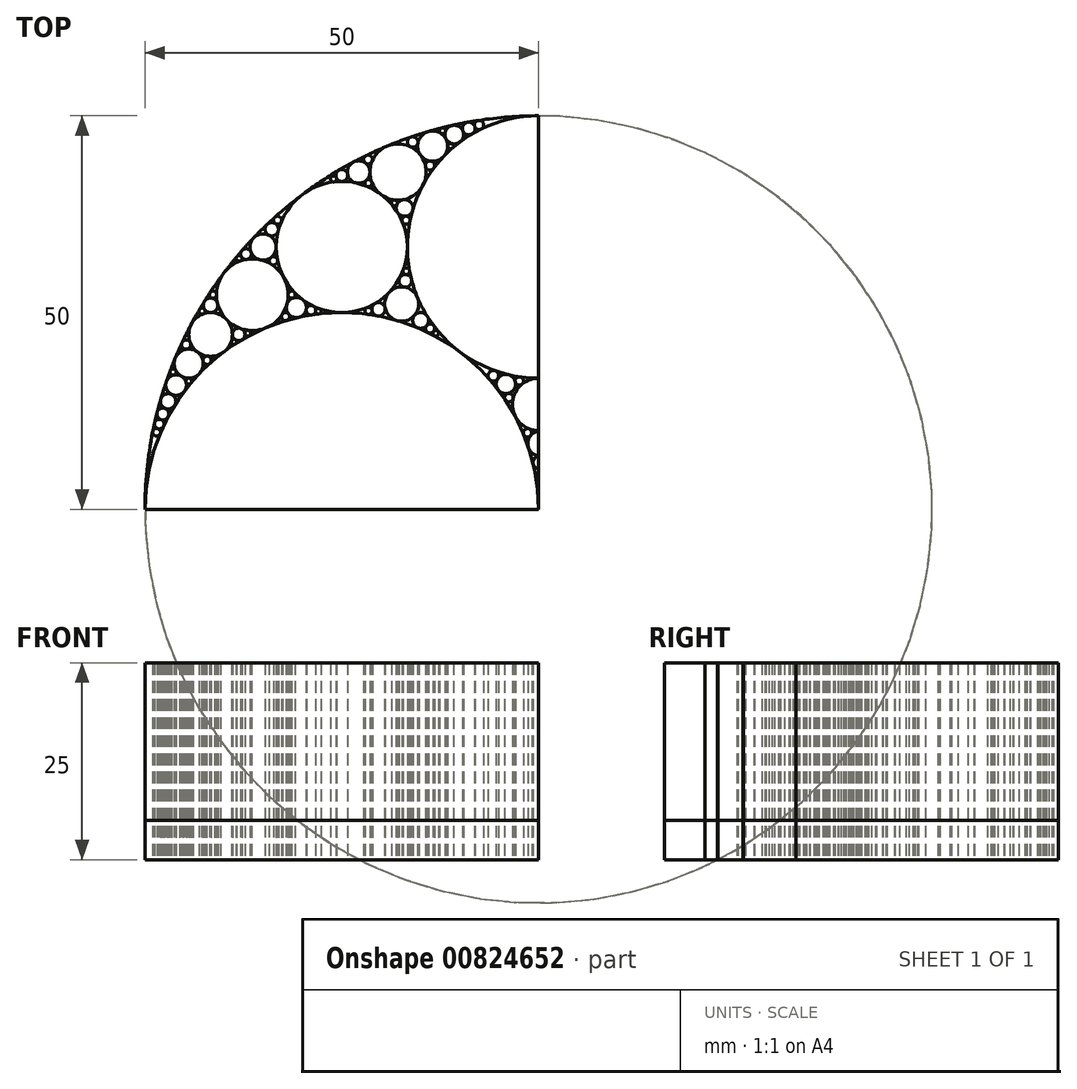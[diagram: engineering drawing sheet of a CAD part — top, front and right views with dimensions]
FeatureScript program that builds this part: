
annotation { "Feature Type Name" : "Feature", "Feature Type Description" : "" }
export const myFeature = defineFeature(function(context is Context, id is Id, definition is map)
    precondition{}
    {
        {
            var Q0;
            Q0=qCreatedBy(makeId("Top.planeOp"),FACE);
            var sketch = newSketch(context, id + "F0", { "sketchPlane" : qUnion([Q0])});
            skCircle(sketch, "E0", {"center": v(-25, 33.33) * mm, "radius": 8.33 * mm});
            skCircle(sketch, "E1", {"center": v(-17.86, 42.86) * mm, "radius": 3.57 * mm});
            skCircle(sketch, "E2", {"center": v(-36.36, 27.27) * mm, "radius": 4.55 * mm});
            skCircle(sketch, "E3", {"center": v(-17.4, 26.09) * mm, "radius": 2.17 * mm});
            skCircle(sketch, "E4", {"center": v(-41.67, 22.22) * mm, "radius": 2.78 * mm});
            skCircle(sketch, "E5", {"center": v(-44.44, 18.52) * mm, "radius": 1.85 * mm});
            skCircle(sketch, "E6", {"center": v(-4.16, 15.93) * mm, "radius": 1.23 * mm});
            skCircle(sketch, "E7", {"center": v(-46.05, 15.79) * mm, "radius": 1.32 * mm});
            skCircle(sketch, "E8", {"center": v(-47.06, 13.73) * mm, "radius": 0.98 * mm});
            skCircle(sketch, "E9", {"center": v(-30.77, 25.64) * mm, "radius": 1.28 * mm});
            skCircle(sketch, "E10", {"center": v(-38.1, 22.22) * mm, "radius": 0.8 * mm});
            skCircle(sketch, "E11", {"center": v(-42.1, 18.95) * mm, "radius": 0.53 * mm});
            skCircle(sketch, "E12", {"center": v(-44.44, 16.3) * mm, "radius": 0.37 * mm});
            skCircle(sketch, "E13", {"center": v(-44.77, 20.93) * mm, "radius": 0.58 * mm});
            skCircle(sketch, "E14", {"center": v(-41.67, 25.93) * mm, "radius": 0.93 * mm});
            skCircle(sketch, "E15", {"center": v(-35, 33.33) * mm, "radius": 1.67 * mm});
            skCircle(sketch, "E16", {"center": v(-20.34, 25.42) * mm, "radius": 0.85 * mm});
            skCircle(sketch, "E17", {"center": v(-14.99, 24) * mm, "radius": 1 * mm});
            skCircle(sketch, "E18", {"center": v(-16.93, 29.03) * mm, "radius": 0.8 * mm});
            skCircle(sketch, "E19", {"center": v(-17.02, 38.3) * mm, "radius": 1.06 * mm});
            skCircle(sketch, "E20", {"center": v(-22.86, 42.86) * mm, "radius": 1.43 * mm});
            skCircle(sketch, "E21", {"center": v(-13.46, 46.15) * mm, "radius": 1.92 * mm});
            skCircle(sketch, "E22", {"center": v(-2.45, 16.32) * mm, "radius": 0.53 * mm});
            skCircle(sketch, "E23", {"center": v(-3.77, 14.2) * mm, "radius": 0.54 * mm});
            skCircle(sketch, "E24", {"center": v(-5.75, 16.98) * mm, "radius": 0.67 * mm});
            skCircle(sketch, "E25", {"center": v(-1.4, 9.73) * mm, "radius": 0.53 * mm});
            skCircle(sketch, "E26", {"center": v(-46.43, 17.46) * mm, "radius": 0.4 * mm});
            skCircle(sketch, "E27", {"center": v(-47.73, 12.12) * mm, "radius": 0.76 * mm});
            skCircle(sketch, "E28", {"center": v(-48.53, 9.8) * mm, "radius": 0.5 * mm});
            skCircle(sketch, "E29", {"center": v(-48.2, 10.84) * mm, "radius": 0.6 * mm});
            skCircle(sketch, "E30", {"center": v(-47.41, 14.94) * mm, "radius": 0.29 * mm});
            skCircle(sketch, "E31", {"center": v(-45.9, 14.2) * mm, "radius": 0.27 * mm});
            skCircle(sketch, "E32", {"center": v(-46.86, 12.55) * mm, "radius": 0.2 * mm});
            skCircle(sketch, "E33", {"center": v(-48.04, 13.04) * mm, "radius": 0.22 * mm});
            skArc(sketch, "E34", {"start": v(0, 50) * mm, "mid": v(-35.36, 35.36) * mm, "end": v(-50, 0) * mm});
            skLineSegment(sketch, "E35", {"start": v(0, 50) * mm, "end": v(0, 0) * mm});
            skArc(sketch, "E36", {"start": v(0, 6.74) * mm, "mid": v(-0.7, 5.95) * mm, "end": v(0, 5.16) * mm});
            skArc(sketch, "E37", {"start": v(0, 9.98) * mm, "mid": v(-1.35, 8.3) * mm, "end": v(0.16, 6.74) * mm});
            skArc(sketch, "E38", {"start": v(0, 16.67) * mm, "mid": v(-3.33, 13.33) * mm, "end": v(0, 10) * mm});
            skArc(sketch, "E39", {"start": v(0, 0) * mm, "mid": v(-25, 25) * mm, "end": v(-50, 0) * mm});
            skPoint(sketch, "E40.second.point", {"position": v(-10, 20) * mm});
            skArc(sketch, "E41", {"start": v(0, 50) * mm, "mid": v(-16.67, 33.33) * mm, "end": v(0, 16.67) * mm});
            skCircle(sketch, "E42", {"center": v(-10.71, 47.62) * mm, "radius": 1.2 * mm});
            skLineSegment(sketch, "E43", {"start": v(0, 0) * mm, "end": v(-50, 0) * mm});
            skCircle(sketch, "E44", {"center": v(-33.9, 35.6) * mm, "radius": 0.85 * mm});
            skCircle(sketch, "E45", {"center": v(-37.16, 32.43) * mm, "radius": 0.68 * mm});
            skCircle(sketch, "E46", {"center": v(-28.92, 25.3) * mm, "radius": 0.6 * mm});
            skCircle(sketch, "E47", {"center": v(-32.14, 24.49) * mm, "radius": 0.51 * mm});
            skCircle(sketch, "E48", {"center": v(-31.36, 27.27) * mm, "radius": 0.45 * mm});
            skCircle(sketch, "E49", {"center": v(-25, 42.42) * mm, "radius": 0.76 * mm});
            skCircle(sketch, "E50", {"center": v(-8.87, 48.39) * mm, "radius": 0.8 * mm});
            skCircle(sketch, "E51", {"center": v(-13.78, 22.98) * mm, "radius": 0.57 * mm});
            skCircle(sketch, "E52", {"center": v(-13.05, 22.38) * mm, "radius": 0.37 * mm});
            skCircle(sketch, "E53", {"center": v(-21.62, 25.23) * mm, "radius": 0.45 * mm});
            skCircle(sketch, "E54", {"center": v(-16.8, 30.25) * mm, "radius": 0.42 * mm});
            skCircle(sketch, "E55", {"center": v(-27.97, 25.17) * mm, "radius": 0.35 * mm});
            skCircle(sketch, "E56", {"center": v(-32.79, 24.04) * mm, "radius": 0.27 * mm});
            skCircle(sketch, "E57", {"center": v(-31.63, 27.9) * mm, "radius": 0.23 * mm});
            skCircle(sketch, "E58", {"center": v(-36.94, 22.39) * mm, "radius": 0.37 * mm});
            skCircle(sketch, "E59", {"center": v(-38.7, 21.3) * mm, "radius": 0.32 * mm});
            skCircle(sketch, "E60", {"center": v(-38.74, 23.08) * mm, "radius": 0.27 * mm});
            skCircle(sketch, "E61", {"center": v(-41.36, 27.27) * mm, "radius": 0.45 * mm});
            skCircle(sketch, "E62", {"center": v(-42.75, 25.2) * mm, "radius": 0.38 * mm});
            skCircle(sketch, "E63", {"center": v(-40.72, 25.15) * mm, "radius": 0.3 * mm});
            skCircle(sketch, "E64", {"center": v(-41.38, 19.21) * mm, "radius": 0.25 * mm});
            skCircle(sketch, "E65", {"center": v(-42.63, 19.42) * mm, "radius": 0.18 * mm});
            skCircle(sketch, "E66", {"center": v(-44.1, 20.53) * mm, "radius": 0.2 * mm});
            skCircle(sketch, "E67", {"center": v(-45.39, 20.39) * mm, "radius": 0.24 * mm});
            skCircle(sketch, "E68", {"center": v(-44.7, 21.79) * mm, "radius": 0.28 * mm});
            skCircle(sketch, "E69", {"center": v(-42.4, 18.26) * mm, "radius": 0.22 * mm});
            skCircle(sketch, "E70", {"center": v(-33.68, 31.58) * mm, "radius": 0.53 * mm});
            skCircle(sketch, "E71", {"center": v(-33.16, 36.73) * mm, "radius": 0.51 * mm});
            skCircle(sketch, "E72", {"center": v(-38.04, 31.88) * mm, "radius": 0.36 * mm});
            skCircle(sketch, "E73", {"center": v(-13.8, 43.68) * mm, "radius": 0.57 * mm});
            skCircle(sketch, "E74", {"center": v(-16, 46.67) * mm, "radius": 0.67 * mm});
            skCircle(sketch, "E75", {"center": v(-12.21, 48.1) * mm, "radius": 0.38 * mm});
            skCircle(sketch, "E76", {"center": v(-11.19, 46.15) * mm, "radius": 0.35 * mm});
            skCircle(sketch, "E77", {"center": v(-7.56, 48.84) * mm, "radius": 0.58 * mm});
            skCircle(sketch, "E78", {"center": v(-21.62, 41.44) * mm, "radius": 0.45 * mm});
            skCircle(sketch, "E79", {"center": v(-18.32, 38.93) * mm, "radius": 0.38 * mm});
            skCircle(sketch, "E80", {"center": v(-21.67, 44.44) * mm, "radius": 0.56 * mm});
            skCircle(sketch, "E81", {"center": v(-26.05, 41.99) * mm, "radius": 0.38 * mm});
            skCircle(sketch, "E82", {"center": v(-16.84, 36.73) * mm, "radius": 0.51 * mm});
            skSolve(sketch);
        }
        {
            var Q0;
            {var subQ0=sQuery(id+"F0.wireOp",EDGE,"E28");var subQ1=makeQuery(id+"F0.imprint","INTERSECT",VERTEX,{"derivedFrom":[subQ0,sQuery(id+"F0.wireOp",EDGE,"E34")]});Q0=makeQuery(id+"F0.imprint","IMPRINT",FACE,{"disambiguationData":[TD([[makeQuery(id+"F0.imprint","IMPRINT",EDGE,{"disambiguationData":[TD([[subQ1,1.0]])],"derivedFrom":subQ0}),1.0]])]});}
            var Q1;
            {var subQ0=sQuery(id+"F0.wireOp",EDGE,"E29");var subQ1=makeQuery(id+"F0.imprint","INTERSECT",VERTEX,{"derivedFrom":[subQ0,sQuery(id+"F0.wireOp",EDGE,"E34")]});Q1=makeQuery(id+"F0.imprint","IMPRINT",FACE,{"disambiguationData":[TD([[makeQuery(id+"F0.imprint","IMPRINT",EDGE,{"disambiguationData":[TD([[subQ1,1.0]])],"derivedFrom":subQ0}),1.0]])]});}
            var Q2;
            {var subQ0=sQuery(id+"F0.wireOp",EDGE,"E27");var subQ4=makeQuery(id+"F0.imprint","INTERSECT",VERTEX,{"derivedFrom":[sQuery(id+"F0.wireOp",EDGE,"E8"),subQ0]});Q2=makeQuery(id+"F0.imprint","IMPRINT",FACE,{"disambiguationData":[TD([[makeQuery(id+"F0.imprint","IMPRINT",EDGE,{"disambiguationData":[TD([[subQ4,1.0]])],"derivedFrom":subQ0}),1.0]])]});}
            var Q3;
            {var subQ0=sQuery(id+"F0.wireOp",EDGE,"E33");var subQ1=makeQuery(id+"F0.imprint","INTERSECT",VERTEX,{"derivedFrom":[subQ0,sQuery(id+"F0.wireOp",EDGE,"E34")]});Q3=makeQuery(id+"F0.imprint","IMPRINT",FACE,{"disambiguationData":[TD([[makeQuery(id+"F0.imprint","IMPRINT",EDGE,{"disambiguationData":[TD([[subQ1,1.0]])],"derivedFrom":subQ0}),1.0]])]});}
            var Q4;
            {var subQ0=sQuery(id+"F0.wireOp",EDGE,"E32");var subQ1=makeQuery(id+"F0.imprint","INTERSECT",VERTEX,{"derivedFrom":[sQuery(id+"F0.wireOp",EDGE,"E8"),subQ0]});Q4=makeQuery(id+"F0.imprint","IMPRINT",FACE,{"disambiguationData":[TD([[makeQuery(id+"F0.imprint","IMPRINT",EDGE,{"disambiguationData":[TD([[subQ1,-1.0]])],"derivedFrom":subQ0}),1.0]])]});}
            var Q5;
            {var subQ4=sQuery(id+"F0.wireOp",EDGE,"E43");Q5=makeQuery(id+"F0.imprint","IMPRINT",FACE,{"disambiguationData":[TD([[makeQuery(id+"F0.imprint","IMPRINT",EDGE,{"derivedFrom":subQ4}),-1.0]])]});}
            var Q6;
            {var subQ0=sQuery(id+"F0.wireOp",EDGE,"E8");var subQ4=makeQuery(id+"F0.imprint","INTERSECT",VERTEX,{"derivedFrom":[sQuery(id+"F0.wireOp",EDGE,"E7"),subQ0]});Q6=makeQuery(id+"F0.imprint","IMPRINT",FACE,{"disambiguationData":[TD([[makeQuery(id+"F0.imprint","IMPRINT",EDGE,{"disambiguationData":[TD([[subQ4,1.0]])],"derivedFrom":subQ0}),1.0]])]});}
            var Q7;
            {var subQ0=sQuery(id+"F0.wireOp",EDGE,"E30");var subQ1=makeQuery(id+"F0.imprint","INTERSECT",VERTEX,{"derivedFrom":[subQ0,sQuery(id+"F0.wireOp",EDGE,"E34")]});Q7=makeQuery(id+"F0.imprint","IMPRINT",FACE,{"disambiguationData":[TD([[makeQuery(id+"F0.imprint","IMPRINT",EDGE,{"disambiguationData":[TD([[subQ1,1.0]])],"derivedFrom":subQ0}),1.0]])]});}
            var Q8;
            {var subQ0=sQuery(id+"F0.wireOp",EDGE,"E31");var subQ1=makeQuery(id+"F0.imprint","INTERSECT",VERTEX,{"derivedFrom":[sQuery(id+"F0.wireOp",EDGE,"E7"),subQ0]});Q8=makeQuery(id+"F0.imprint","IMPRINT",FACE,{"disambiguationData":[TD([[makeQuery(id+"F0.imprint","IMPRINT",EDGE,{"disambiguationData":[TD([[subQ1,-1.0]])],"derivedFrom":subQ0}),1.0]])]});}
            var Q9;
            {var subQ0=sQuery(id+"F0.wireOp",EDGE,"E7");var subQ4=makeQuery(id+"F0.imprint","INTERSECT",VERTEX,{"derivedFrom":[sQuery(id+"F0.wireOp",EDGE,"E5"),subQ0]});Q9=makeQuery(id+"F0.imprint","IMPRINT",FACE,{"disambiguationData":[TD([[makeQuery(id+"F0.imprint","IMPRINT",EDGE,{"disambiguationData":[TD([[subQ4,1.0]])],"derivedFrom":subQ0}),1.0]])]});}
            var Q10;
            {var subQ0=sQuery(id+"F0.wireOp",EDGE,"E26");var subQ1=makeQuery(id+"F0.imprint","INTERSECT",VERTEX,{"derivedFrom":[subQ0,sQuery(id+"F0.wireOp",EDGE,"E34")]});Q10=makeQuery(id+"F0.imprint","IMPRINT",FACE,{"disambiguationData":[TD([[makeQuery(id+"F0.imprint","IMPRINT",EDGE,{"disambiguationData":[TD([[subQ1,1.0]])],"derivedFrom":subQ0}),1.0]])]});}
            var Q11;
            {var subQ0=sQuery(id+"F0.wireOp",EDGE,"E12");var subQ1=makeQuery(id+"F0.imprint","INTERSECT",VERTEX,{"derivedFrom":[sQuery(id+"F0.wireOp",EDGE,"E5"),subQ0]});Q11=makeQuery(id+"F0.imprint","IMPRINT",FACE,{"disambiguationData":[TD([[makeQuery(id+"F0.imprint","IMPRINT",EDGE,{"disambiguationData":[TD([[subQ1,-1.0]])],"derivedFrom":subQ0}),1.0]])]});}
            var Q12;
            {var subQ0=sQuery(id+"F0.wireOp",EDGE,"E5");var subQ8=makeQuery(id+"F0.imprint","INTERSECT",VERTEX,{"derivedFrom":[subQ0,sQuery(id+"F0.wireOp",EDGE,"E65")]});Q12=makeQuery(id+"F0.imprint","IMPRINT",FACE,{"disambiguationData":[TD([[makeQuery(id+"F0.imprint","IMPRINT",EDGE,{"disambiguationData":[TD([[subQ8,1.0]])],"derivedFrom":subQ0}),1.0]])]});}
            var Q13;
            {var subQ0=sQuery(id+"F0.wireOp",EDGE,"E67");var subQ1=makeQuery(id+"F0.imprint","INTERSECT",VERTEX,{"derivedFrom":[sQuery(id+"F0.wireOp",EDGE,"E34"),subQ0]});Q13=makeQuery(id+"F0.imprint","IMPRINT",FACE,{"disambiguationData":[TD([[makeQuery(id+"F0.imprint","IMPRINT",EDGE,{"disambiguationData":[TD([[subQ1,1.0]])],"derivedFrom":subQ0}),1.0]])]});}
            var Q14;
            {var subQ0=sQuery(id+"F0.wireOp",EDGE,"E13");var subQ5=makeQuery(id+"F0.imprint","INTERSECT",VERTEX,{"derivedFrom":[sQuery(id+"F0.wireOp",EDGE,"E4"),subQ0]});Q14=makeQuery(id+"F0.imprint","IMPRINT",FACE,{"disambiguationData":[TD([[makeQuery(id+"F0.imprint","IMPRINT",EDGE,{"disambiguationData":[TD([[subQ5,-1.0]])],"derivedFrom":subQ0}),1.0]])]});}
            var Q15;
            {var subQ0=sQuery(id+"F0.wireOp",EDGE,"E66");var subQ1=makeQuery(id+"F0.imprint","INTERSECT",VERTEX,{"derivedFrom":[sQuery(id+"F0.wireOp",EDGE,"E4"),subQ0]});Q15=makeQuery(id+"F0.imprint","IMPRINT",FACE,{"disambiguationData":[TD([[makeQuery(id+"F0.imprint","IMPRINT",EDGE,{"disambiguationData":[TD([[subQ1,-1.0]])],"derivedFrom":subQ0}),1.0]])]});}
            var Q16;
            {var subQ0=sQuery(id+"F0.wireOp",EDGE,"E68");var subQ1=makeQuery(id+"F0.imprint","INTERSECT",VERTEX,{"derivedFrom":[sQuery(id+"F0.wireOp",EDGE,"E34"),subQ0]});Q16=makeQuery(id+"F0.imprint","IMPRINT",FACE,{"disambiguationData":[TD([[makeQuery(id+"F0.imprint","IMPRINT",EDGE,{"disambiguationData":[TD([[subQ1,1.0]])],"derivedFrom":subQ0}),1.0]])]});}
            var Q17;
            {var subQ0=sQuery(id+"F0.wireOp",EDGE,"E11");var subQ4=makeQuery(id+"F0.imprint","INTERSECT",VERTEX,{"derivedFrom":[sQuery(id+"F0.wireOp",EDGE,"E4"),subQ0]});Q17=makeQuery(id+"F0.imprint","IMPRINT",FACE,{"disambiguationData":[TD([[makeQuery(id+"F0.imprint","IMPRINT",EDGE,{"disambiguationData":[TD([[subQ4,1.0]])],"derivedFrom":subQ0}),1.0]])]});}
            var Q18;
            {var subQ0=sQuery(id+"F0.wireOp",EDGE,"E65");var subQ1=makeQuery(id+"F0.imprint","INTERSECT",VERTEX,{"derivedFrom":[sQuery(id+"F0.wireOp",EDGE,"E4"),subQ0]});Q18=makeQuery(id+"F0.imprint","IMPRINT",FACE,{"disambiguationData":[TD([[makeQuery(id+"F0.imprint","IMPRINT",EDGE,{"disambiguationData":[TD([[subQ1,-1.0]])],"derivedFrom":subQ0}),1.0]])]});}
            var Q19;
            {var subQ0=sQuery(id+"F0.wireOp",EDGE,"E4");var subQ8=makeQuery(id+"F0.imprint","INTERSECT",VERTEX,{"derivedFrom":[subQ0,sQuery(id+"F0.wireOp",EDGE,"E60")]});Q19=makeQuery(id+"F0.imprint","IMPRINT",FACE,{"disambiguationData":[TD([[makeQuery(id+"F0.imprint","IMPRINT",EDGE,{"disambiguationData":[TD([[subQ8,1.0]])],"derivedFrom":subQ0}),1.0]])]});}
            var Q20;
            {var subQ0=sQuery(id+"F0.wireOp",EDGE,"E64");var subQ1=makeQuery(id+"F0.imprint","INTERSECT",VERTEX,{"derivedFrom":[sQuery(id+"F0.wireOp",EDGE,"E4"),subQ0]});Q20=makeQuery(id+"F0.imprint","IMPRINT",FACE,{"disambiguationData":[TD([[makeQuery(id+"F0.imprint","IMPRINT",EDGE,{"disambiguationData":[TD([[subQ1,-1.0]])],"derivedFrom":subQ0}),1.0]])]});}
            var Q21;
            {var subQ0=sQuery(id+"F0.wireOp",EDGE,"E69");var subQ1=makeQuery(id+"F0.imprint","INTERSECT",VERTEX,{"derivedFrom":[sQuery(id+"F0.wireOp",EDGE,"E5"),subQ0]});Q21=makeQuery(id+"F0.imprint","IMPRINT",FACE,{"disambiguationData":[TD([[makeQuery(id+"F0.imprint","IMPRINT",EDGE,{"disambiguationData":[TD([[subQ1,1.0]])],"derivedFrom":subQ0}),1.0]])]});}
            var Q22;
            {var subQ0=sQuery(id+"F0.wireOp",EDGE,"E59");var subQ1=makeQuery(id+"F0.imprint","INTERSECT",VERTEX,{"derivedFrom":[sQuery(id+"F0.wireOp",EDGE,"E4"),subQ0]});Q22=makeQuery(id+"F0.imprint","IMPRINT",FACE,{"disambiguationData":[TD([[makeQuery(id+"F0.imprint","IMPRINT",EDGE,{"disambiguationData":[TD([[subQ1,1.0]])],"derivedFrom":subQ0}),1.0]])]});}
            var Q23;
            {var subQ0=sQuery(id+"F0.wireOp",EDGE,"E10");var subQ4=makeQuery(id+"F0.imprint","INTERSECT",VERTEX,{"derivedFrom":[sQuery(id+"F0.wireOp",EDGE,"E2"),subQ0]});Q23=makeQuery(id+"F0.imprint","IMPRINT",FACE,{"disambiguationData":[TD([[makeQuery(id+"F0.imprint","IMPRINT",EDGE,{"disambiguationData":[TD([[subQ4,1.0]])],"derivedFrom":subQ0}),1.0]])]});}
            var Q24;
            {var subQ0=sQuery(id+"F0.wireOp",EDGE,"E60");var subQ1=makeQuery(id+"F0.imprint","INTERSECT",VERTEX,{"derivedFrom":[sQuery(id+"F0.wireOp",EDGE,"E2"),subQ0]});Q24=makeQuery(id+"F0.imprint","IMPRINT",FACE,{"disambiguationData":[TD([[makeQuery(id+"F0.imprint","IMPRINT",EDGE,{"disambiguationData":[TD([[subQ1,-1.0]])],"derivedFrom":subQ0}),1.0]])]});}
            var Q25;
            {var subQ0=sQuery(id+"F0.wireOp",EDGE,"E58");var subQ1=makeQuery(id+"F0.imprint","INTERSECT",VERTEX,{"derivedFrom":[sQuery(id+"F0.wireOp",EDGE,"E2"),subQ0]});Q25=makeQuery(id+"F0.imprint","IMPRINT",FACE,{"disambiguationData":[TD([[makeQuery(id+"F0.imprint","IMPRINT",EDGE,{"disambiguationData":[TD([[subQ1,-1.0]])],"derivedFrom":subQ0}),1.0]])]});}
            var Q26;
            {var subQ0=sQuery(id+"F0.wireOp",EDGE,"E63");var subQ1=makeQuery(id+"F0.imprint","INTERSECT",VERTEX,{"derivedFrom":[sQuery(id+"F0.wireOp",EDGE,"E2"),subQ0]});Q26=makeQuery(id+"F0.imprint","IMPRINT",FACE,{"disambiguationData":[TD([[makeQuery(id+"F0.imprint","IMPRINT",EDGE,{"disambiguationData":[TD([[subQ1,-1.0]])],"derivedFrom":subQ0}),1.0]])]});}
            var Q27;
            {var subQ0=sQuery(id+"F0.wireOp",EDGE,"E62");var subQ1=makeQuery(id+"F0.imprint","INTERSECT",VERTEX,{"derivedFrom":[sQuery(id+"F0.wireOp",EDGE,"E34"),subQ0]});Q27=makeQuery(id+"F0.imprint","IMPRINT",FACE,{"disambiguationData":[TD([[makeQuery(id+"F0.imprint","IMPRINT",EDGE,{"disambiguationData":[TD([[subQ1,1.0]])],"derivedFrom":subQ0}),1.0]])]});}
            var Q28;
            {var subQ0=sQuery(id+"F0.wireOp",EDGE,"E14");var subQ5=makeQuery(id+"F0.imprint","INTERSECT",VERTEX,{"derivedFrom":[sQuery(id+"F0.wireOp",EDGE,"E2"),subQ0]});Q28=makeQuery(id+"F0.imprint","IMPRINT",FACE,{"disambiguationData":[TD([[makeQuery(id+"F0.imprint","IMPRINT",EDGE,{"disambiguationData":[TD([[subQ5,-1.0]])],"derivedFrom":subQ0}),1.0]])]});}
            var Q29;
            {var subQ0=sQuery(id+"F0.wireOp",EDGE,"E61");var subQ1=makeQuery(id+"F0.imprint","INTERSECT",VERTEX,{"derivedFrom":[sQuery(id+"F0.wireOp",EDGE,"E34"),subQ0]});Q29=makeQuery(id+"F0.imprint","IMPRINT",FACE,{"disambiguationData":[TD([[makeQuery(id+"F0.imprint","IMPRINT",EDGE,{"disambiguationData":[TD([[subQ1,1.0]])],"derivedFrom":subQ0}),1.0]])]});}
            var Q30;
            {var subQ0=sQuery(id+"F0.wireOp",EDGE,"E2");var subQ8=makeQuery(id+"F0.imprint","INTERSECT",VERTEX,{"derivedFrom":[subQ0,sQuery(id+"F0.wireOp",EDGE,"E57")]});Q30=makeQuery(id+"F0.imprint","IMPRINT",FACE,{"disambiguationData":[TD([[makeQuery(id+"F0.imprint","IMPRINT",EDGE,{"disambiguationData":[TD([[subQ8,1.0]])],"derivedFrom":subQ0}),1.0]])]});}
            var Q31;
            {var subQ0=sQuery(id+"F0.wireOp",EDGE,"E56");var subQ1=makeQuery(id+"F0.imprint","INTERSECT",VERTEX,{"derivedFrom":[sQuery(id+"F0.wireOp",EDGE,"E2"),subQ0]});Q31=makeQuery(id+"F0.imprint","IMPRINT",FACE,{"disambiguationData":[TD([[makeQuery(id+"F0.imprint","IMPRINT",EDGE,{"disambiguationData":[TD([[subQ1,1.0]])],"derivedFrom":subQ0}),1.0]])]});}
            var Q32;
            {var subQ0=sQuery(id+"F0.wireOp",EDGE,"E47");var subQ1=makeQuery(id+"F0.imprint","INTERSECT",VERTEX,{"derivedFrom":[sQuery(id+"F0.wireOp",EDGE,"E2"),subQ0]});Q32=makeQuery(id+"F0.imprint","IMPRINT",FACE,{"disambiguationData":[TD([[makeQuery(id+"F0.imprint","IMPRINT",EDGE,{"disambiguationData":[TD([[subQ1,1.0]])],"derivedFrom":subQ0}),1.0]])]});}
            var Q33;
            {var subQ0=sQuery(id+"F0.wireOp",EDGE,"E9");var subQ5=makeQuery(id+"F0.imprint","INTERSECT",VERTEX,{"derivedFrom":[sQuery(id+"F0.wireOp",EDGE,"E0"),subQ0]});Q33=makeQuery(id+"F0.imprint","IMPRINT",FACE,{"disambiguationData":[TD([[makeQuery(id+"F0.imprint","IMPRINT",EDGE,{"disambiguationData":[TD([[subQ5,-1.0]])],"derivedFrom":subQ0}),1.0]])]});}
            var Q34;
            {var subQ0=sQuery(id+"F0.wireOp",EDGE,"E46");var subQ1=makeQuery(id+"F0.imprint","INTERSECT",VERTEX,{"derivedFrom":[sQuery(id+"F0.wireOp",EDGE,"E0"),subQ0]});Q34=makeQuery(id+"F0.imprint","IMPRINT",FACE,{"disambiguationData":[TD([[makeQuery(id+"F0.imprint","IMPRINT",EDGE,{"disambiguationData":[TD([[subQ1,-1.0]])],"derivedFrom":subQ0}),1.0]])]});}
            var Q35;
            {var subQ0=sQuery(id+"F0.wireOp",EDGE,"E55");var subQ1=makeQuery(id+"F0.imprint","INTERSECT",VERTEX,{"derivedFrom":[sQuery(id+"F0.wireOp",EDGE,"E0"),subQ0]});Q35=makeQuery(id+"F0.imprint","IMPRINT",FACE,{"disambiguationData":[TD([[makeQuery(id+"F0.imprint","IMPRINT",EDGE,{"disambiguationData":[TD([[subQ1,-1.0]])],"derivedFrom":subQ0}),1.0]])]});}
            var Q36;
            {var subQ0=sQuery(id+"F0.wireOp",EDGE,"E48");var subQ1=makeQuery(id+"F0.imprint","INTERSECT",VERTEX,{"derivedFrom":[sQuery(id+"F0.wireOp",EDGE,"E0"),subQ0]});Q36=makeQuery(id+"F0.imprint","IMPRINT",FACE,{"disambiguationData":[TD([[makeQuery(id+"F0.imprint","IMPRINT",EDGE,{"disambiguationData":[TD([[subQ1,-1.0]])],"derivedFrom":subQ0}),1.0]])]});}
            var Q37;
            {var subQ0=sQuery(id+"F0.wireOp",EDGE,"E57");var subQ1=makeQuery(id+"F0.imprint","INTERSECT",VERTEX,{"derivedFrom":[sQuery(id+"F0.wireOp",EDGE,"E0"),subQ0]});Q37=makeQuery(id+"F0.imprint","IMPRINT",FACE,{"disambiguationData":[TD([[makeQuery(id+"F0.imprint","IMPRINT",EDGE,{"disambiguationData":[TD([[subQ1,-1.0]])],"derivedFrom":subQ0}),1.0]])]});}
            var Q38;
            {var subQ0=sQuery(id+"F0.wireOp",EDGE,"E53");var subQ1=makeQuery(id+"F0.imprint","INTERSECT",VERTEX,{"derivedFrom":[sQuery(id+"F0.wireOp",EDGE,"E0"),subQ0]});Q38=makeQuery(id+"F0.imprint","IMPRINT",FACE,{"disambiguationData":[TD([[makeQuery(id+"F0.imprint","IMPRINT",EDGE,{"disambiguationData":[TD([[subQ1,1.0]])],"derivedFrom":subQ0}),1.0]])]});}
            var Q39;
            {var subQ0=sQuery(id+"F0.wireOp",EDGE,"E16");var subQ1=makeQuery(id+"F0.imprint","INTERSECT",VERTEX,{"derivedFrom":[sQuery(id+"F0.wireOp",EDGE,"E0"),subQ0]});Q39=makeQuery(id+"F0.imprint","IMPRINT",FACE,{"disambiguationData":[TD([[makeQuery(id+"F0.imprint","IMPRINT",EDGE,{"disambiguationData":[TD([[subQ1,1.0]])],"derivedFrom":subQ0}),1.0]])]});}
            var Q40;
            {var subQ0=sQuery(id+"F0.wireOp",EDGE,"E3");var subQ4=makeQuery(id+"F0.imprint","INTERSECT",VERTEX,{"derivedFrom":[subQ0,sQuery(id+"F0.wireOp",EDGE,"E18")]});Q40=makeQuery(id+"F0.imprint","IMPRINT",FACE,{"disambiguationData":[TD([[makeQuery(id+"F0.imprint","IMPRINT",EDGE,{"disambiguationData":[TD([[subQ4,1.0]])],"derivedFrom":subQ0}),1.0]])]});}
            var Q41;
            {var subQ1=sQuery(id+"F0.wireOp",EDGE,"E17");var subQ5=makeQuery(id+"F0.imprint","INTERSECT",VERTEX,{"derivedFrom":[sQuery(id+"F0.wireOp",EDGE,"E3"),subQ1]});Q41=makeQuery(id+"F0.imprint","IMPRINT",FACE,{"disambiguationData":[TD([[makeQuery(id+"F0.imprint","IMPRINT",EDGE,{"disambiguationData":[TD([[subQ5,1.0]])],"derivedFrom":subQ1}),1.0]])]});}
            var Q42;
            {var subQ0=sQuery(id+"F0.wireOp",EDGE,"E51");var subQ1=makeQuery(id+"F0.imprint","INTERSECT",VERTEX,{"derivedFrom":[sQuery(id+"F0.wireOp",EDGE,"E17"),subQ0]});Q42=makeQuery(id+"F0.imprint","IMPRINT",FACE,{"disambiguationData":[TD([[makeQuery(id+"F0.imprint","IMPRINT",EDGE,{"disambiguationData":[TD([[subQ1,1.0]])],"derivedFrom":subQ0}),1.0]])]});}
            var Q43;
            {var subQ0=sQuery(id+"F0.wireOp",EDGE,"E52");var subQ1=makeQuery(id+"F0.imprint","INTERSECT",VERTEX,{"derivedFrom":[sQuery(id+"F0.wireOp",EDGE,"E41"),subQ0]});Q43=makeQuery(id+"F0.imprint","IMPRINT",FACE,{"disambiguationData":[TD([[makeQuery(id+"F0.imprint","IMPRINT",EDGE,{"disambiguationData":[TD([[subQ1,-1.0]])],"derivedFrom":subQ0}),1.0]])]});}
            var Q44;
            {var subQ0=sQuery(id+"F0.wireOp",EDGE,"E18");var subQ2=sQuery(id+"F0.wireOp",EDGE,"E41");var subQ6=makeQuery(id+"F0.imprint","INTERSECT",VERTEX,{"disambiguationData":[OD(0.0)],"derivedFrom":[subQ0,subQ2]});Q44=makeQuery(id+"F0.imprint","IMPRINT",FACE,{"disambiguationData":[TD([[makeQuery(id+"F0.imprint","IMPRINT",EDGE,{"disambiguationData":[TD([[subQ6,-1.0]])],"derivedFrom":subQ0}),1.0]])]});}
            var Q45;
            {var subQ0=sQuery(id+"F0.wireOp",EDGE,"E54");var subQ1=makeQuery(id+"F0.imprint","INTERSECT",VERTEX,{"derivedFrom":[sQuery(id+"F0.wireOp",EDGE,"E0"),subQ0]});Q45=makeQuery(id+"F0.imprint","IMPRINT",FACE,{"disambiguationData":[TD([[makeQuery(id+"F0.imprint","IMPRINT",EDGE,{"disambiguationData":[TD([[subQ1,1.0]])],"derivedFrom":subQ0}),1.0]])]});}
            var Q46;
            {var subQ0=sQuery(id+"F0.wireOp",EDGE,"E0");var subQ17=makeQuery(id+"F0.imprint","INTERSECT",VERTEX,{"derivedFrom":[subQ0,sQuery(id+"F0.wireOp",EDGE,"E82")]});Q46=makeQuery(id+"F0.imprint","IMPRINT",FACE,{"disambiguationData":[TD([[makeQuery(id+"F0.imprint","IMPRINT",EDGE,{"disambiguationData":[TD([[subQ17,1.0]])],"derivedFrom":subQ0}),1.0]])]});}
            var Q47;
            {var subQ0=sQuery(id+"F0.wireOp",EDGE,"E15");var subQ5=makeQuery(id+"F0.imprint","INTERSECT",VERTEX,{"derivedFrom":[sQuery(id+"F0.wireOp",EDGE,"E0"),subQ0]});Q47=makeQuery(id+"F0.imprint","IMPRINT",FACE,{"disambiguationData":[TD([[makeQuery(id+"F0.imprint","IMPRINT",EDGE,{"disambiguationData":[TD([[subQ5,-1.0]])],"derivedFrom":subQ0}),1.0]])]});}
            var Q48;
            {var subQ0=sQuery(id+"F0.wireOp",EDGE,"E45");var subQ1=makeQuery(id+"F0.imprint","INTERSECT",VERTEX,{"derivedFrom":[sQuery(id+"F0.wireOp",EDGE,"E34"),subQ0]});Q48=makeQuery(id+"F0.imprint","IMPRINT",FACE,{"disambiguationData":[TD([[makeQuery(id+"F0.imprint","IMPRINT",EDGE,{"disambiguationData":[TD([[subQ1,1.0]])],"derivedFrom":subQ0}),1.0]])]});}
            var Q49;
            {var subQ0=sQuery(id+"F0.wireOp",EDGE,"E72");var subQ1=makeQuery(id+"F0.imprint","INTERSECT",VERTEX,{"derivedFrom":[sQuery(id+"F0.wireOp",EDGE,"E34"),subQ0]});Q49=makeQuery(id+"F0.imprint","IMPRINT",FACE,{"disambiguationData":[TD([[makeQuery(id+"F0.imprint","IMPRINT",EDGE,{"disambiguationData":[TD([[subQ1,1.0]])],"derivedFrom":subQ0}),1.0]])]});}
            var Q50;
            {var subQ0=sQuery(id+"F0.wireOp",EDGE,"E70");var subQ1=makeQuery(id+"F0.imprint","INTERSECT",VERTEX,{"derivedFrom":[sQuery(id+"F0.wireOp",EDGE,"E0"),subQ0]});Q50=makeQuery(id+"F0.imprint","IMPRINT",FACE,{"disambiguationData":[TD([[makeQuery(id+"F0.imprint","IMPRINT",EDGE,{"disambiguationData":[TD([[subQ1,-1.0]])],"derivedFrom":subQ0}),1.0]])]});}
            var Q51;
            {var subQ0=sQuery(id+"F0.wireOp",EDGE,"E44");var subQ1=makeQuery(id+"F0.imprint","INTERSECT",VERTEX,{"derivedFrom":[sQuery(id+"F0.wireOp",EDGE,"E34"),subQ0]});Q51=makeQuery(id+"F0.imprint","IMPRINT",FACE,{"disambiguationData":[TD([[makeQuery(id+"F0.imprint","IMPRINT",EDGE,{"disambiguationData":[TD([[subQ1,1.0]])],"derivedFrom":subQ0}),1.0]])]});}
            var Q52;
            {var subQ0=sQuery(id+"F0.wireOp",EDGE,"E71");var subQ1=makeQuery(id+"F0.imprint","INTERSECT",VERTEX,{"derivedFrom":[sQuery(id+"F0.wireOp",EDGE,"E34"),subQ0]});Q52=makeQuery(id+"F0.imprint","IMPRINT",FACE,{"disambiguationData":[TD([[makeQuery(id+"F0.imprint","IMPRINT",EDGE,{"disambiguationData":[TD([[subQ1,-1.0]])],"derivedFrom":subQ0}),1.0]])]});}
            var Q53;
            {var subQ0=sQuery(id+"F0.wireOp",EDGE,"E81");var subQ1=makeQuery(id+"F0.imprint","INTERSECT",VERTEX,{"derivedFrom":[sQuery(id+"F0.wireOp",EDGE,"E0"),subQ0]});Q53=makeQuery(id+"F0.imprint","IMPRINT",FACE,{"disambiguationData":[TD([[makeQuery(id+"F0.imprint","IMPRINT",EDGE,{"disambiguationData":[TD([[subQ1,1.0]])],"derivedFrom":subQ0}),1.0]])]});}
            var Q54;
            {var subQ0=sQuery(id+"F0.wireOp",EDGE,"E49");var subQ1=makeQuery(id+"F0.imprint","INTERSECT",VERTEX,{"derivedFrom":[sQuery(id+"F0.wireOp",EDGE,"E34"),subQ0]});Q54=makeQuery(id+"F0.imprint","IMPRINT",FACE,{"disambiguationData":[TD([[makeQuery(id+"F0.imprint","IMPRINT",EDGE,{"disambiguationData":[TD([[subQ1,1.0]])],"derivedFrom":subQ0}),1.0]])]});}
            var Q55;
            {var subQ0=sQuery(id+"F0.wireOp",EDGE,"E20");var subQ5=makeQuery(id+"F0.imprint","INTERSECT",VERTEX,{"derivedFrom":[sQuery(id+"F0.wireOp",EDGE,"E1"),subQ0]});Q55=makeQuery(id+"F0.imprint","IMPRINT",FACE,{"disambiguationData":[TD([[makeQuery(id+"F0.imprint","IMPRINT",EDGE,{"disambiguationData":[TD([[subQ5,-1.0]])],"derivedFrom":subQ0}),1.0]])]});}
            var Q56;
            {var subQ0=sQuery(id+"F0.wireOp",EDGE,"E78");var subQ1=makeQuery(id+"F0.imprint","INTERSECT",VERTEX,{"derivedFrom":[sQuery(id+"F0.wireOp",EDGE,"E1"),subQ0]});Q56=makeQuery(id+"F0.imprint","IMPRINT",FACE,{"disambiguationData":[TD([[makeQuery(id+"F0.imprint","IMPRINT",EDGE,{"disambiguationData":[TD([[subQ1,-1.0]])],"derivedFrom":subQ0}),1.0]])]});}
            var Q57;
            {var subQ0=sQuery(id+"F0.wireOp",EDGE,"E80");var subQ1=makeQuery(id+"F0.imprint","INTERSECT",VERTEX,{"derivedFrom":[sQuery(id+"F0.wireOp",EDGE,"E34"),subQ0]});Q57=makeQuery(id+"F0.imprint","IMPRINT",FACE,{"disambiguationData":[TD([[makeQuery(id+"F0.imprint","IMPRINT",EDGE,{"disambiguationData":[TD([[subQ1,-1.0]])],"derivedFrom":subQ0}),1.0]])]});}
            var Q58;
            {var subQ0=sQuery(id+"F0.wireOp",EDGE,"E1");var subQ8=makeQuery(id+"F0.imprint","INTERSECT",VERTEX,{"derivedFrom":[subQ0,sQuery(id+"F0.wireOp",EDGE,"E21")]});Q58=makeQuery(id+"F0.imprint","IMPRINT",FACE,{"disambiguationData":[TD([[makeQuery(id+"F0.imprint","IMPRINT",EDGE,{"disambiguationData":[TD([[subQ8,1.0]])],"derivedFrom":subQ0}),1.0]])]});}
            var Q59;
            {var subQ0=sQuery(id+"F0.wireOp",EDGE,"E79");var subQ1=makeQuery(id+"F0.imprint","INTERSECT",VERTEX,{"derivedFrom":[sQuery(id+"F0.wireOp",EDGE,"E0"),subQ0]});Q59=makeQuery(id+"F0.imprint","IMPRINT",FACE,{"disambiguationData":[TD([[makeQuery(id+"F0.imprint","IMPRINT",EDGE,{"disambiguationData":[TD([[subQ1,1.0]])],"derivedFrom":subQ0}),1.0]])]});}
            var Q60;
            {var subQ0=sQuery(id+"F0.wireOp",EDGE,"E19");var subQ5=makeQuery(id+"F0.imprint","INTERSECT",VERTEX,{"derivedFrom":[sQuery(id+"F0.wireOp",EDGE,"E1"),subQ0]});Q60=makeQuery(id+"F0.imprint","IMPRINT",FACE,{"disambiguationData":[TD([[makeQuery(id+"F0.imprint","IMPRINT",EDGE,{"disambiguationData":[TD([[subQ5,-1.0]])],"derivedFrom":subQ0}),1.0]])]});}
            var Q61;
            {var subQ0=sQuery(id+"F0.wireOp",EDGE,"E82");var subQ1=makeQuery(id+"F0.imprint","INTERSECT",VERTEX,{"derivedFrom":[sQuery(id+"F0.wireOp",EDGE,"E0"),subQ0]});Q61=makeQuery(id+"F0.imprint","IMPRINT",FACE,{"disambiguationData":[TD([[makeQuery(id+"F0.imprint","IMPRINT",EDGE,{"disambiguationData":[TD([[subQ1,1.0]])],"derivedFrom":subQ0}),1.0]])]});}
            var Q62;
            {var subQ0=sQuery(id+"F0.wireOp",EDGE,"E73");var subQ1=makeQuery(id+"F0.imprint","INTERSECT",VERTEX,{"derivedFrom":[sQuery(id+"F0.wireOp",EDGE,"E1"),subQ0]});Q62=makeQuery(id+"F0.imprint","IMPRINT",FACE,{"disambiguationData":[TD([[makeQuery(id+"F0.imprint","IMPRINT",EDGE,{"disambiguationData":[TD([[subQ1,1.0]])],"derivedFrom":subQ0}),1.0]])]});}
            var Q63;
            {var subQ0=sQuery(id+"F0.wireOp",EDGE,"E21");var subQ4=makeQuery(id+"F0.imprint","INTERSECT",VERTEX,{"derivedFrom":[subQ0,sQuery(id+"F0.wireOp",EDGE,"E42")]});Q63=makeQuery(id+"F0.imprint","IMPRINT",FACE,{"disambiguationData":[TD([[makeQuery(id+"F0.imprint","IMPRINT",EDGE,{"disambiguationData":[TD([[subQ4,1.0]])],"derivedFrom":subQ0}),1.0]])]});}
            var Q64;
            {var subQ0=sQuery(id+"F0.wireOp",EDGE,"E74");var subQ1=makeQuery(id+"F0.imprint","INTERSECT",VERTEX,{"derivedFrom":[sQuery(id+"F0.wireOp",EDGE,"E34"),subQ0]});Q64=makeQuery(id+"F0.imprint","IMPRINT",FACE,{"disambiguationData":[TD([[makeQuery(id+"F0.imprint","IMPRINT",EDGE,{"disambiguationData":[TD([[subQ1,-1.0]])],"derivedFrom":subQ0}),1.0]])]});}
            var Q65;
            {var subQ0=sQuery(id+"F0.wireOp",EDGE,"E75");var subQ1=makeQuery(id+"F0.imprint","INTERSECT",VERTEX,{"derivedFrom":[sQuery(id+"F0.wireOp",EDGE,"E34"),subQ0]});Q65=makeQuery(id+"F0.imprint","IMPRINT",FACE,{"disambiguationData":[TD([[makeQuery(id+"F0.imprint","IMPRINT",EDGE,{"disambiguationData":[TD([[subQ1,-1.0]])],"derivedFrom":subQ0}),1.0]])]});}
            var Q66;
            {var subQ0=sQuery(id+"F0.wireOp",EDGE,"E76");var subQ1=makeQuery(id+"F0.imprint","INTERSECT",VERTEX,{"derivedFrom":[sQuery(id+"F0.wireOp",EDGE,"E21"),subQ0]});Q66=makeQuery(id+"F0.imprint","IMPRINT",FACE,{"disambiguationData":[TD([[makeQuery(id+"F0.imprint","IMPRINT",EDGE,{"disambiguationData":[TD([[subQ1,1.0]])],"derivedFrom":subQ0}),1.0]])]});}
            var Q67;
            {var subQ0=sQuery(id+"F0.wireOp",EDGE,"E42");var subQ4=makeQuery(id+"F0.imprint","INTERSECT",VERTEX,{"derivedFrom":[sQuery(id+"F0.wireOp",EDGE,"E34"),subQ0]});Q67=makeQuery(id+"F0.imprint","IMPRINT",FACE,{"disambiguationData":[TD([[makeQuery(id+"F0.imprint","IMPRINT",EDGE,{"disambiguationData":[TD([[subQ4,1.0]])],"derivedFrom":subQ0}),1.0]])]});}
            var Q68;
            {var subQ0=sQuery(id+"F0.wireOp",EDGE,"E50");var subQ1=makeQuery(id+"F0.imprint","INTERSECT",VERTEX,{"derivedFrom":[sQuery(id+"F0.wireOp",EDGE,"E34"),subQ0]});Q68=makeQuery(id+"F0.imprint","IMPRINT",FACE,{"disambiguationData":[TD([[makeQuery(id+"F0.imprint","IMPRINT",EDGE,{"disambiguationData":[TD([[subQ1,1.0]])],"derivedFrom":subQ0}),1.0]])]});}
            var Q69;
            {var subQ0=sQuery(id+"F0.wireOp",EDGE,"E77");var subQ1=makeQuery(id+"F0.imprint","INTERSECT",VERTEX,{"derivedFrom":[sQuery(id+"F0.wireOp",EDGE,"E34"),subQ0]});Q69=makeQuery(id+"F0.imprint","IMPRINT",FACE,{"disambiguationData":[TD([[makeQuery(id+"F0.imprint","IMPRINT",EDGE,{"disambiguationData":[TD([[subQ1,-1.0]])],"derivedFrom":subQ0}),1.0]])]});}
            var Q70;
            {var subQ0=sQuery(id+"F0.wireOp",EDGE,"E41");var subQ6=sQuery(id+"F0.wireOp",EDGE,"E17");var subQ20=makeQuery(id+"F0.imprint","INTERSECT",VERTEX,{"disambiguationData":[OD(0.0)],"derivedFrom":[subQ6,subQ0]});Q70=makeQuery(id+"F0.imprint","IMPRINT",FACE,{"disambiguationData":[TD([[makeQuery(id+"F0.imprint","IMPRINT",EDGE,{"disambiguationData":[TD([[subQ20,1.0]])],"derivedFrom":subQ6}),-1.0]])]});}
            var Q71;
            {var subQ0=sQuery(id+"F0.wireOp",EDGE,"E24");var subQ1=makeQuery(id+"F0.imprint","INTERSECT",VERTEX,{"derivedFrom":[subQ0,sQuery(id+"F0.wireOp",EDGE,"E39")]});Q71=makeQuery(id+"F0.imprint","IMPRINT",FACE,{"disambiguationData":[TD([[makeQuery(id+"F0.imprint","IMPRINT",EDGE,{"disambiguationData":[TD([[subQ1,1.0]])],"derivedFrom":subQ0}),1.0]])]});}
            var Q72;
            {var subQ0=sQuery(id+"F0.wireOp",EDGE,"E6");var subQ4=makeQuery(id+"F0.imprint","INTERSECT",VERTEX,{"derivedFrom":[subQ0,sQuery(id+"F0.wireOp",EDGE,"E41")]});Q72=makeQuery(id+"F0.imprint","IMPRINT",FACE,{"disambiguationData":[TD([[makeQuery(id+"F0.imprint","IMPRINT",EDGE,{"disambiguationData":[TD([[subQ4,1.0]])],"derivedFrom":subQ0}),1.0]])]});}
            var Q73;
            {var subQ0=sQuery(id+"F0.wireOp",EDGE,"E22");var subQ1=makeQuery(id+"F0.imprint","INTERSECT",VERTEX,{"derivedFrom":[sQuery(id+"F0.wireOp",EDGE,"E6"),subQ0]});Q73=makeQuery(id+"F0.imprint","IMPRINT",FACE,{"disambiguationData":[TD([[makeQuery(id+"F0.imprint","IMPRINT",EDGE,{"disambiguationData":[TD([[subQ1,1.0]])],"derivedFrom":subQ0}),1.0]])]});}
            var Q74;
            {var subQ0=sQuery(id+"F0.wireOp",EDGE,"E23");var subQ1=makeQuery(id+"F0.imprint","INTERSECT",VERTEX,{"derivedFrom":[sQuery(id+"F0.wireOp",EDGE,"E6"),subQ0]});Q74=makeQuery(id+"F0.imprint","IMPRINT",FACE,{"disambiguationData":[TD([[makeQuery(id+"F0.imprint","IMPRINT",EDGE,{"disambiguationData":[TD([[subQ1,-1.0]])],"derivedFrom":subQ0}),1.0]])]});}
            var Q75;
            {var subQ0=sQuery(id+"F0.wireOp",EDGE,"E38");var subQ3=makeQuery(id+"F0.imprint","INTERSECT",VERTEX,{"derivedFrom":[sQuery(id+"F0.wireOp",EDGE,"E22"),subQ0]});Q75=makeQuery(id+"F0.imprint","IMPRINT",FACE,{"disambiguationData":[TD([[makeQuery(id+"F0.imprint","IMPRINT",EDGE,{"disambiguationData":[TD([[subQ3,-1.0]])],"derivedFrom":subQ0}),1.0]])]});}
            var Q76;
            {var subQ0=sQuery(id+"F0.wireOp",EDGE,"E25");var subQ1=makeQuery(id+"F0.imprint","INTERSECT",VERTEX,{"derivedFrom":[subQ0,sQuery(id+"F0.wireOp",EDGE,"E39")]});Q76=makeQuery(id+"F0.imprint","IMPRINT",FACE,{"disambiguationData":[TD([[makeQuery(id+"F0.imprint","IMPRINT",EDGE,{"disambiguationData":[TD([[subQ1,1.0]])],"derivedFrom":subQ0}),1.0]])]});}
            var Q77;
            {var subQ0=sQuery(id+"F0.wireOp",EDGE,"E37");var subQ1=sQuery(id+"F0.wireOp",EDGE,"E35");var subQ2=makeQuery(id+"F0.imprint","INTERSECT",VERTEX,{"disambiguationData":[OD(0.0)],"derivedFrom":[subQ1,subQ0]});Q77=makeQuery(id+"F0.imprint","IMPRINT",FACE,{"disambiguationData":[TD([[makeQuery(id+"F0.imprint","IMPRINT",EDGE,{"disambiguationData":[TD([[subQ2,-1.0]])],"derivedFrom":subQ1}),-1.0]])]});}
            var Q78;
            {var subQ0=sQuery(id+"F0.wireOp",EDGE,"E36");var subQ1=sQuery(id+"F0.wireOp",EDGE,"E35");var subQ2=makeQuery(id+"F0.imprint","INTERSECT",VERTEX,{"disambiguationData":[OD(0.0)],"derivedFrom":[subQ1,subQ0]});Q78=makeQuery(id+"F0.imprint","IMPRINT",FACE,{"disambiguationData":[TD([[makeQuery(id+"F0.imprint","IMPRINT",EDGE,{"disambiguationData":[TD([[subQ2,-1.0]])],"derivedFrom":subQ1}),-1.0]])]});}
            extrude(context, id + "F1", {"entities" : qUnion([Q0, Q1, Q2, Q3, Q4, Q5, Q6, Q7, Q8, Q9, Q10, Q11, Q12, Q13, Q14, Q15, Q16, Q17, Q18, Q19, Q20, Q21, Q22, Q23, Q24, Q25, Q26, Q27, Q28, Q29, Q30, Q31, Q32, Q33, Q34, Q35, Q36, Q37, Q38, Q39, Q40, Q41, Q42, Q43, Q44, Q45, Q46, Q47, Q48, Q49, Q50, Q51, Q52, Q53, Q54, Q55, Q56, Q57, Q58, Q59, Q60, Q61, Q62, Q63, Q64, Q65, Q66, Q67, Q68, Q69, Q70, Q71, Q72, Q73, Q74, Q75, Q76, Q77, Q78]), "depth" : 25 * mm, "offsetDistance" : 25 * mm});
        }
        {
            var Q0;
            Q0=qCreatedBy(makeId("Top.planeOp"),FACE);
            var sketch = newSketch(context, id + "F2", { "sketchPlane" : qUnion([Q0])});
            skLineSegment(sketch, "E83", {"start": v(0, 0) * mm, "end": v(0, 50) * mm});
            skLineSegment(sketch, "E84", {"start": v(0, 0) * mm, "end": v(-50, 0) * mm});
            skLineSegment(sketch, "E85", {"start": v(-50, 0) * mm, "end": v(-50, -16.6) * mm, "construction": true});
            skArc(sketch, "E86", {"start": v(0, 50) * mm, "mid": v(-35.36, 35.36) * mm, "end": v(-50, 0) * mm});
            skSolve(sketch);
        }
        {
            var Q0;
            Q0 = qSketchRegion(id + "F2", true);
            extrude(context, id + "F3", {"entities" : qUnion([Q0]), "depth" : 5 * mm, "offsetDistance" : 25 * mm});
        }
    });
